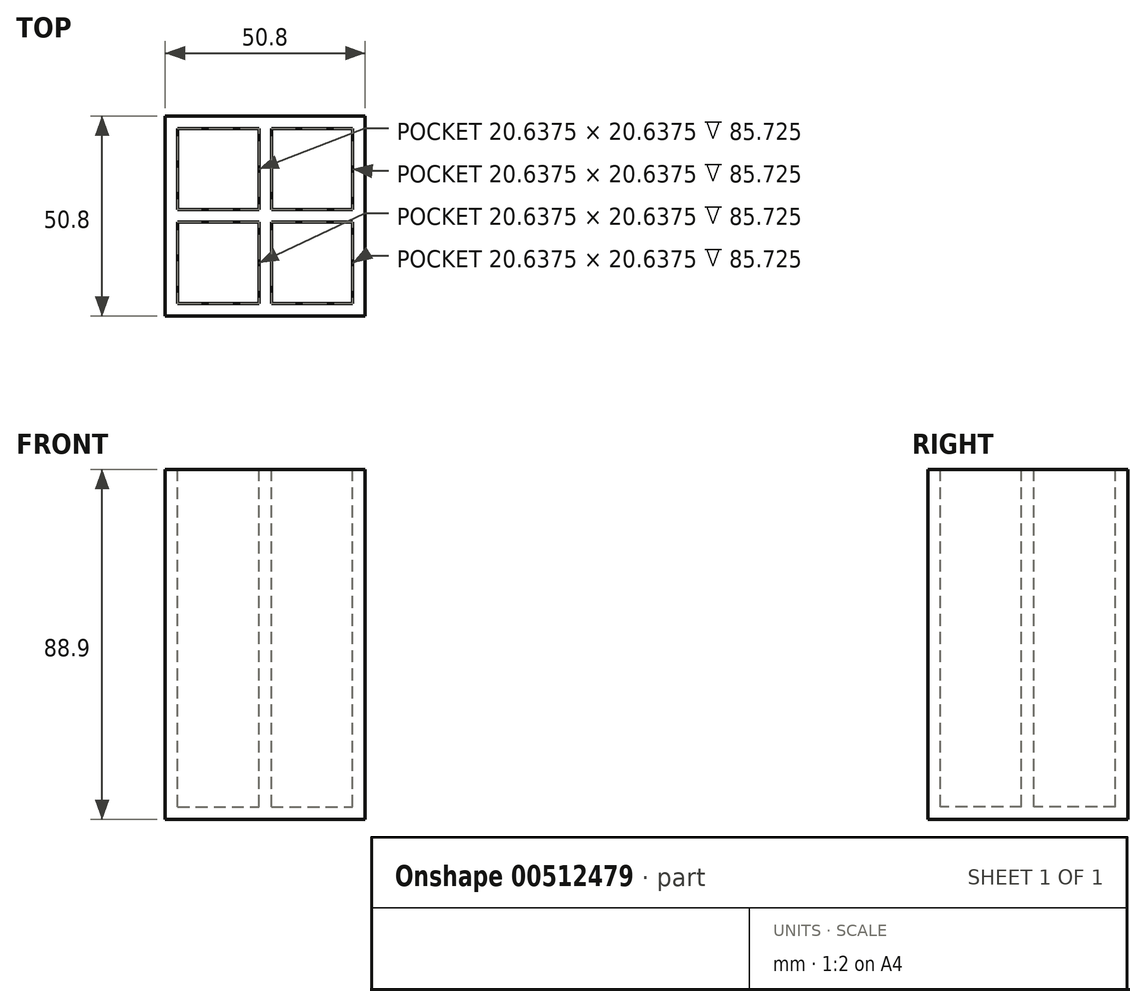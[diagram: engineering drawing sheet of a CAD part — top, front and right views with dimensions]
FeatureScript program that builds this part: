
annotation { "Feature Type Name" : "Feature", "Feature Type Description" : "" }
export const myFeature = defineFeature(function(context is Context, id is Id, definition is map)
    precondition{}
    {
        {
            var Q0;
            Q0=qCreatedBy(makeId("Front.planeOp"),FACE);
            var sketch = newSketch(context, id + "F0", { "sketchPlane" : qUnion([Q0])});
            skLineSegment(sketch, "E0.bottom", {"start": v(-25.4, 44.45) * mm, "end": v(25.4, 44.45) * mm});
            skLineSegment(sketch, "E0.top", {"start": v(-25.4, -44.45) * mm, "end": v(25.4, -44.45) * mm});
            skLineSegment(sketch, "E0.left", {"start": v(-25.4, 44.45) * mm, "end": v(-25.4, -44.45) * mm});
            skLineSegment(sketch, "E0.right", {"start": v(25.4, 44.45) * mm, "end": v(25.4, -44.45) * mm});
            skPoint(sketch, "E0.middle", {"position": v(0, 0) * mm});
            skSolve(sketch);
        }
        {
            var Q0;
            Q0=makeQuery(id+"F0.imprint","IMPRINT",FACE,{"disambiguationData":[TD([[makeQuery(id+"F0.imprint","IMPRINT",EDGE,{"derivedFrom":sQuery(id+"F0.wireOp",EDGE,"E0.bottom")}),-1.0]])]});
            extrude(context, id + "F1", {"entities" : qUnion([Q0]), "depth" : 57.15 * mm});
        }
        {
            var Q0;
            Q0=makeQuery(id+"F1.opExtrude","SWEPT_FACE",FACE,{"disambiguationData":[OSD([sQuery(id+"F0.wireOp",EDGE,"E0.bottom")])]});
            var sketch = newSketch(context, id + "F2", { "sketchPlane" : qUnion([Q0])});
            skLineSegment(sketch, "E1.bottom", {"start": v(-22.22, -3.18) * mm, "end": v(-1.59, -3.18) * mm});
            skLineSegment(sketch, "E1.top", {"start": v(-22.22, -23.81) * mm, "end": v(-1.59, -23.81) * mm});
            skLineSegment(sketch, "E1.left", {"start": v(-22.22, -3.18) * mm, "end": v(-22.22, -23.81) * mm});
            skLineSegment(sketch, "E1.right", {"start": v(-1.59, -3.17) * mm, "end": v(-1.59, -23.81) * mm});
            skSolve(sketch);
        }
        {
            var Q0;
            Q0=makeQuery(id+"F2.imprint","IMPRINT",FACE,{"disambiguationData":[TD([[makeQuery(id+"F2.imprint","IMPRINT",EDGE,{"derivedFrom":sQuery(id+"F2.wireOp",EDGE,"E1.bottom")}),-1.0]])]});
            extrude(context, id + "F3", {"entities" : qUnion([Q0]), "operationType" : NewBodyOperationType.REMOVE, "oppositeDirection" : true, "depth" : 85.72 * mm});
        }
        {
            var Q0;
            Q0=makeQuery(id+"F1.opExtrude","SWEPT_FACE",FACE,{"disambiguationData":[OSD([sQuery(id+"F0.wireOp",EDGE,"E0.bottom")])]});
            var sketch = newSketch(context, id + "F4", { "sketchPlane" : qUnion([Q0])});
            skLineSegment(sketch, "E2.bottom", {"start": v(1.59, -3.18) * mm, "end": v(22.23, -3.18) * mm});
            skLineSegment(sketch, "E2.top", {"start": v(1.59, -23.81) * mm, "end": v(22.23, -23.81) * mm});
            skLineSegment(sketch, "E2.left", {"start": v(1.59, -3.18) * mm, "end": v(1.59, -23.81) * mm});
            skLineSegment(sketch, "E2.right", {"start": v(22.23, -3.17) * mm, "end": v(22.23, -23.81) * mm});
            skSolve(sketch);
        }
        {
            var Q0;
            Q0=makeQuery(id+"F4.imprint","IMPRINT",FACE,{"disambiguationData":[TD([[makeQuery(id+"F4.imprint","IMPRINT",EDGE,{"derivedFrom":sQuery(id+"F4.wireOp",EDGE,"E2.bottom")}),-1.0]])]});
            extrude(context, id + "F5", {"entities" : qUnion([Q0]), "operationType" : NewBodyOperationType.REMOVE, "oppositeDirection" : true, "depth" : 85.72 * mm});
        }
        {
            var Q0;
            Q0=makeQuery(id+"F1.opExtrude","SWEPT_FACE",FACE,{"disambiguationData":[OSD([sQuery(id+"F0.wireOp",EDGE,"E0.bottom")])]});
            var sketch = newSketch(context, id + "F6", { "sketchPlane" : qUnion([Q0])});
            skLineSegment(sketch, "E3.bottom", {"start": v(-22.22, -26.99) * mm, "end": v(-1.59, -26.99) * mm});
            skLineSegment(sketch, "E3.top", {"start": v(-22.22, -47.63) * mm, "end": v(-1.59, -47.63) * mm});
            skLineSegment(sketch, "E3.left", {"start": v(-22.22, -26.99) * mm, "end": v(-22.22, -47.63) * mm});
            skLineSegment(sketch, "E3.right", {"start": v(-1.59, -26.99) * mm, "end": v(-1.59, -47.63) * mm});
            skSolve(sketch);
        }
        {
            var Q0;
            Q0=makeQuery(id+"F6.imprint","IMPRINT",FACE,{"disambiguationData":[TD([[makeQuery(id+"F6.imprint","IMPRINT",EDGE,{"derivedFrom":sQuery(id+"F6.wireOp",EDGE,"E3.bottom")}),-1.0]])]});
            extrude(context, id + "F7", {"entities" : qUnion([Q0]), "operationType" : NewBodyOperationType.REMOVE, "oppositeDirection" : true, "depth" : 85.72 * mm});
        }
        {
            var Q0;
            Q0=makeQuery(id+"F1.opExtrude","SWEPT_FACE",FACE,{"disambiguationData":[OSD([sQuery(id+"F0.wireOp",EDGE,"E0.bottom")])]});
            var sketch = newSketch(context, id + "F8", { "sketchPlane" : qUnion([Q0])});
            skLineSegment(sketch, "E4.bottom", {"start": v(1.59, -26.99) * mm, "end": v(22.23, -26.99) * mm});
            skLineSegment(sketch, "E4.top", {"start": v(1.59, -47.63) * mm, "end": v(22.23, -47.63) * mm});
            skLineSegment(sketch, "E4.left", {"start": v(1.59, -26.99) * mm, "end": v(1.59, -47.63) * mm});
            skLineSegment(sketch, "E4.right", {"start": v(22.23, -26.99) * mm, "end": v(22.23, -47.63) * mm});
            skSolve(sketch);
        }
        {
            var Q0;
            Q0=makeQuery(id+"F8.imprint","IMPRINT",FACE,{"disambiguationData":[TD([[makeQuery(id+"F8.imprint","IMPRINT",EDGE,{"derivedFrom":sQuery(id+"F8.wireOp",EDGE,"E4.bottom")}),-1.0]])]});
            extrude(context, id + "F9", {"entities" : qUnion([Q0]), "operationType" : NewBodyOperationType.REMOVE, "oppositeDirection" : true, "depth" : 85.72 * mm});
        }
        {
            var Q0;
            Q0=makeQuery(id+"F1.opExtrude","SWEPT_FACE",FACE,{"disambiguationData":[OSD([sQuery(id+"F0.wireOp",EDGE,"E0.bottom")])]});
            var sketch = newSketch(context, id + "F10", { "sketchPlane" : qUnion([Q0])});
            skLineSegment(sketch, "E5", {"start": v(-25.4, -50.8) * mm, "end": v(25.4, -50.8) * mm});
            skSolve(sketch);
        }
        {
            var Q0;
            {var subQ0=sQuery(id+"F10.wireOp",EDGE,"E5");Q0=makeQuery(id+"F10.imprint","IMPRINT",FACE,{"disambiguationData":[TD([[makeQuery(id+"F10.imprint","IMPRINT",EDGE,{"derivedFrom":subQ0}),-1.0]])]});}
            extrude(context, id + "F11", {"entities" : qUnion([Q0]), "operationType" : NewBodyOperationType.REMOVE, "oppositeDirection" : true, "depth" : 88.9 * mm});
        }
    });
